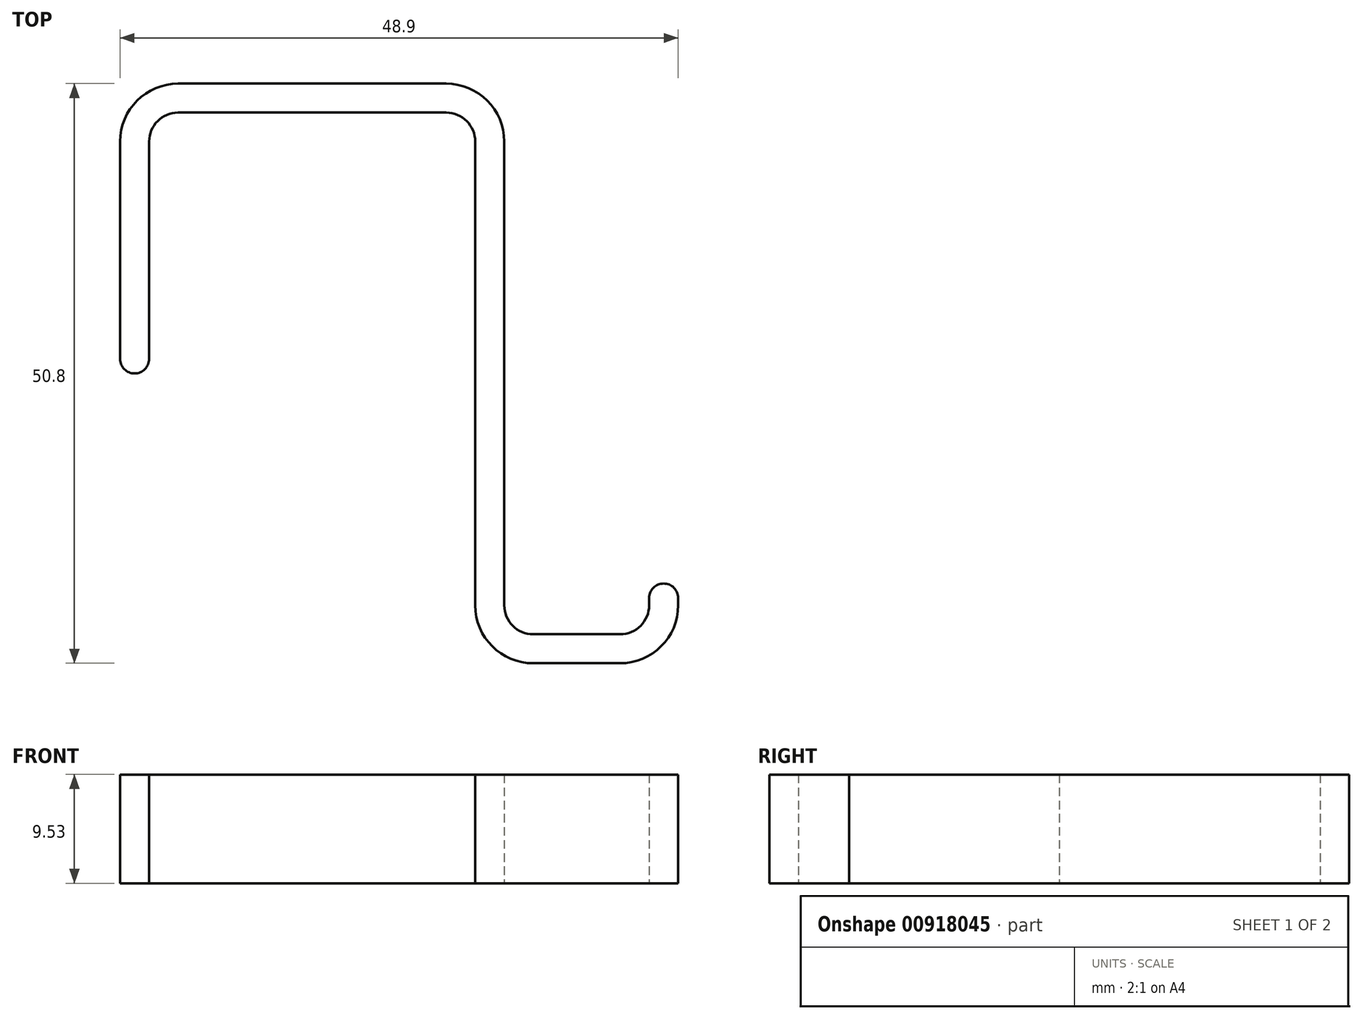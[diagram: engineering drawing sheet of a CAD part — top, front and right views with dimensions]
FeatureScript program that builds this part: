
annotation { "Feature Type Name" : "Feature", "Feature Type Description" : "" }
export const myFeature = defineFeature(function(context is Context, id is Id, definition is map)
    precondition{}
    {
        {
            var Q0;
            Q0=qCreatedBy(makeId("Top.planeOp"),FACE);
            var sketch = newSketch(context, id + "F0", { "sketchPlane" : qUnion([Q0])});
            skLineSegment(sketch, "E0", {"start": v(0, 0) * mm, "end": v(-28.58, 0) * mm});
            skLineSegment(sketch, "E1", {"start": v(-28.58, 0) * mm, "end": v(-28.58, -22.86) * mm});
            skLineSegment(sketch, "E2", {"start": v(-28.57, -22.86) * mm, "end": v(-31.12, -22.86) * mm});
            skLineSegment(sketch, "E3", {"start": v(-31.12, -22.86) * mm, "end": v(-31.12, 2.54) * mm});
            skLineSegment(sketch, "E4", {"start": v(-31.12, 2.54) * mm, "end": v(2.54, 2.54) * mm});
            skLineSegment(sketch, "E5", {"start": v(2.54, 2.54) * mm, "end": v(2.54, -45.72) * mm});
            skLineSegment(sketch, "E6", {"start": v(2.54, -45.72) * mm, "end": v(15.24, -45.72) * mm});
            skLineSegment(sketch, "E7", {"start": v(15.24, -45.72) * mm, "end": v(15.24, -41.27) * mm});
            skLineSegment(sketch, "E8", {"start": v(15.24, -41.27) * mm, "end": v(17.78, -41.27) * mm});
            skLineSegment(sketch, "E9", {"start": v(17.78, -41.27) * mm, "end": v(17.78, -48.26) * mm});
            skLineSegment(sketch, "E10", {"start": v(17.78, -48.26) * mm, "end": v(0, -48.26) * mm});
            skLineSegment(sketch, "E11", {"start": v(0, -48.26) * mm, "end": v(0, 0) * mm});
            skSolve(sketch);
        }
        {
            var Q0;
            Q0 = qSketchRegion(id + "F0", true);
            extrude(context, id + "F1", {"entities" : qUnion([Q0]), "depth" : 9.52 * mm, "offsetDistance" : 25.4 * mm});
        }
        {
            var Q0;
            Q0=makeQuery(id+"F1.opExtrude","SWEPT_EDGE",EDGE,{"disambiguationData":[OSD([sQuery(id+"F0.wireOp",EDGE,"E6"),sQuery(id+"F0.wireOp",EDGE,"E7")])]});
            var Q1;
            Q1=makeQuery(id+"F1.opExtrude","SWEPT_EDGE",EDGE,{"disambiguationData":[OSD([sQuery(id+"F0.wireOp",EDGE,"E5"),sQuery(id+"F0.wireOp",EDGE,"E6")])]});
            var Q2;
            Q2=makeQuery(id+"F1.opExtrude","SWEPT_EDGE",EDGE,{"disambiguationData":[OSD([sQuery(id+"F0.wireOp",EDGE,"E0"),sQuery(id+"F0.wireOp",EDGE,"E1")])]});
            var Q3;
            Q3=makeQuery(id+"F1.opExtrude","SWEPT_EDGE",EDGE,{"disambiguationData":[OSD([sQuery(id+"F0.wireOp",EDGE,"E0"),sQuery(id+"F0.wireOp",EDGE,"E11")])]});
            fillet(context, id + "F2", {"entities" : qUnion([Q0, Q1, Q2, Q3]), "radius" : 2.54 * mm, "tangentPropagation" : true, "allowEdgeOverflow" : false});
        }
        {
            var Q0;
            Q0=makeQuery(id+"F1.opExtrude","SWEPT_EDGE",EDGE,{"disambiguationData":[OSD([sQuery(id+"F0.wireOp",EDGE,"E9"),sQuery(id+"F0.wireOp",EDGE,"E10")])]});
            var Q1;
            Q1=makeQuery(id+"F1.opExtrude","SWEPT_EDGE",EDGE,{"disambiguationData":[OSD([sQuery(id+"F0.wireOp",EDGE,"E10"),sQuery(id+"F0.wireOp",EDGE,"E11")])]});
            var Q2;
            Q2=makeQuery(id+"F1.opExtrude","SWEPT_EDGE",EDGE,{"disambiguationData":[OSD([sQuery(id+"F0.wireOp",EDGE,"E4"),sQuery(id+"F0.wireOp",EDGE,"E5")])]});
            var Q3;
            Q3=makeQuery(id+"F1.opExtrude","SWEPT_EDGE",EDGE,{"disambiguationData":[OSD([sQuery(id+"F0.wireOp",EDGE,"E3"),sQuery(id+"F0.wireOp",EDGE,"E4")])]});
            fillet(context, id + "F3", {"entities" : qUnion([Q0, Q1, Q2, Q3]), "radius" : 5.08 * mm, "tangentPropagation" : true, "allowEdgeOverflow" : false});
        }
        {
            var Q0;
            Q0=makeQuery(id+"F1.opExtrude","SWEPT_EDGE",EDGE,{"disambiguationData":[OSD([sQuery(id+"F0.wireOp",EDGE,"E2"),sQuery(id+"F0.wireOp",EDGE,"E3")])]});
            var Q1;
            Q1=makeQuery(id+"F1.opExtrude","SWEPT_EDGE",EDGE,{"disambiguationData":[OSD([sQuery(id+"F0.wireOp",EDGE,"E1"),sQuery(id+"F0.wireOp",EDGE,"E2")])]});
            var Q2;
            Q2=makeQuery(id+"F1.opExtrude","SWEPT_EDGE",EDGE,{"disambiguationData":[OSD([sQuery(id+"F0.wireOp",EDGE,"E7"),sQuery(id+"F0.wireOp",EDGE,"E8")])]});
            var Q3;
            Q3=makeQuery(id+"F1.opExtrude","SWEPT_EDGE",EDGE,{"disambiguationData":[OSD([sQuery(id+"F0.wireOp",EDGE,"E8"),sQuery(id+"F0.wireOp",EDGE,"E9")])]});
            fillet(context, id + "F4", {"entities" : qUnion([Q0, Q1, Q2, Q3]), "radius" : 1.27 * mm, "tangentPropagation" : true, "allowEdgeOverflow" : false});
        }
    });
